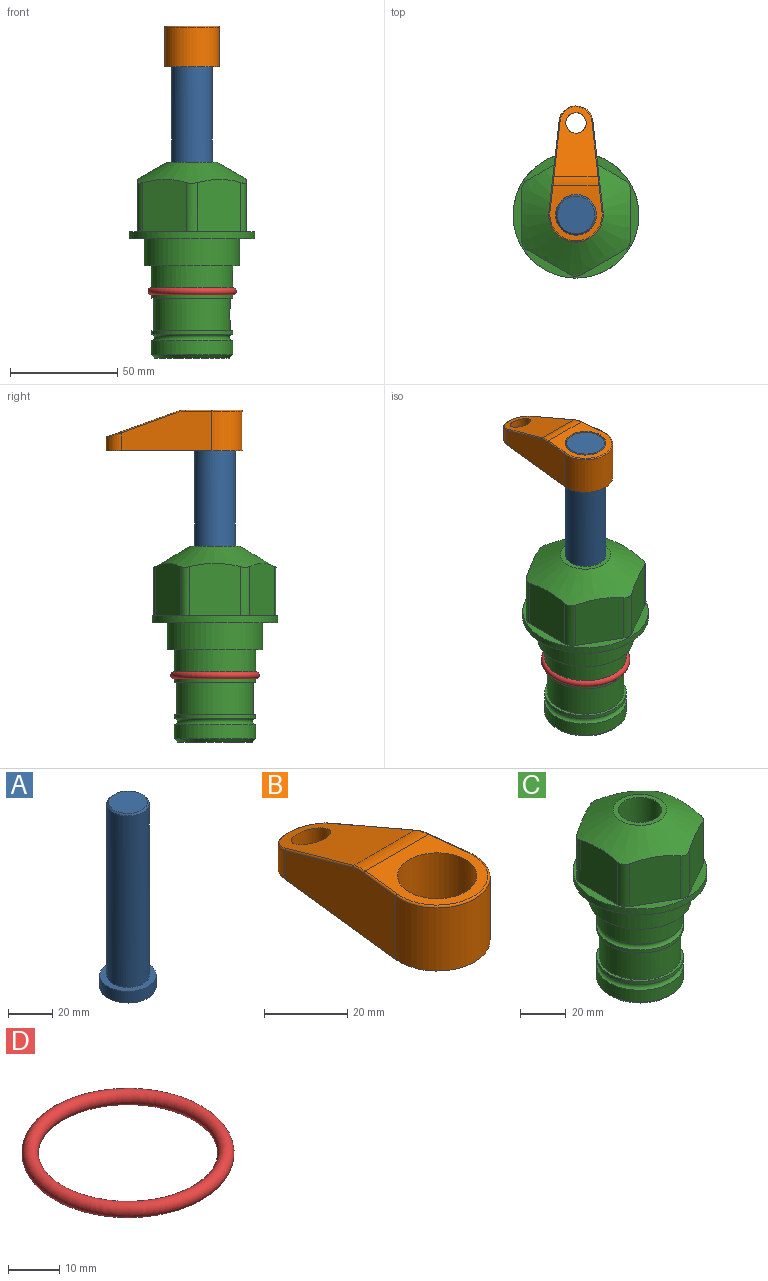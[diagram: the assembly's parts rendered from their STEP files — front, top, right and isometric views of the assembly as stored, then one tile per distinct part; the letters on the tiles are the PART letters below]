
ASSEMBLY  parts=4 mates=2
PART A: 6 faces, bbox 25.4x25.4x101.6 mm
  f0: plane 17.46x17.46mm, normal (0,0,1), area 239.5mm2, adj f5
  f1: plane 25.4x25.4mm, normal (0,0,-1), area 506.7mm2, adj f2
  f2: cylinder r=12.7mm len=25.4mm, axis (0,0,1), area 506.7mm2, adj f1,f3
  f3: plane 25.4x25.4mm, normal (0,0,1), area 221.7mm2, adj f2,f4
  f4: cylinder r=9.53mm len=94.46mm, axis (0,0,1), area 5653mm2, adj f3,f5
  f5: cone r=8.73mm half-angle=45deg, axis (0,0,-1), area 64.4mm2, adj f0,f4
PART B: 44 faces, bbox 27.5x64.5x19.1 mm
  f0: plane 2.3x0.95mm, normal (0,0,-1), area 1mm2, adj f25,f30,f34
  f1: plane 63.5x25.4mm, normal (0,0,-1), area 561.7mm2, adj f2,f3,f4,f5,f6,f7,f19,f20
  f2: cylinder r=12.7mm len=25.4mm, axis (0,0,-1), area 792.2mm2, adj f1,f3,f5,f13
  f3: plane 42.33x18.54mm, normal (0.99,0.11,0), area 647mm2, adj f1,f2,f4,f11,f12,f14
  f4: cylinder r=7.94mm len=15.78mm, axis (0,0,-1), area 158.6mm2, adj f1,f3,f5,f16
  f5: plane 42.33x18.54mm, normal (-0.99,0.11,0), area 647mm2, adj f1,f2,f4,f15,f17,f18
  f6: cylinder r=9.53mm len=19.05mm, axis (0,0,-1), area 1140.1mm2, adj f1,f8
  f7: cylinder r=4.76mm len=10.98mm, axis (0,0,-1), area 276.1mm2, adj f1,f9
  f8: plane 25.83x24.38mm, normal (0,0,1), area 262.2mm2, adj f6,f10,f11,f13,f15
  f9: plane 32.49x20.55mm, normal (0,0.34,0.94), area 489.9mm2, adj f7,f10,f14,f16,f18
  f10: cylinder r=12.7mm len=21.49mm, axis (-1,0,0), area 93.2mm2, adj f8,f9,f12,f17
  f11: cylinder r=0.51mm len=12.34mm, axis (0.11,-0.99,0), area 9.9mm2, adj f3,f8,f12,f13
  f12: bspline ~7.62x1.64mm, area 3.5mm2, adj f3,f10,f11,f14
  f13: torus R=12.19mm, axis (0,0,1), area 33.6mm2, adj f2,f8,f11,f15
  f14: cylinder r=0.51mm len=26.01mm, axis (0.1,-0.93,0.34), area 21.6mm2, adj f3,f9,f12,f16
  f15: cylinder r=0.51mm len=12.34mm, axis (0.11,0.99,0), area 9.9mm2, adj f5,f8,f13,f17
  f16: bspline ~15.78x7.05mm, area 15.7mm2, adj f4,f9,f14,f18
  f17: bspline ~7.62x1.64mm, area 3.5mm2, adj f5,f10,f15,f18
  f18: cylinder r=0.51mm len=26.01mm, axis (0.1,0.93,-0.34), area 21.6mm2, adj f5,f9,f16,f17
  f19: plane 21.6x14.29mm, normal (-0.99,-0.11,0), area 242.6mm2, adj f1,f26,f28,f34,f36,f38
  f20: plane 21.6x14.29mm, normal (0.99,-0.11,0), area 242.6mm2, adj f1,f27,f29,f37,f39,f41
  f21: cylinder r=12.7mm len=14.29mm, axis (0,0,-1), area 173.2mm2, adj f1,f26,f27,f30,f31,f33
  f22: cylinder r=7.94mm len=7.63mm, axis (0,0,-1), area 53.8mm2, adj f1,f28,f29,f42
  f23: plane 2.3x0.95mm, normal (0,0,-1), area 1mm2, adj f25,f33,f37
  f24: plane 17.94x12.32mm, normal (0,-0.34,-0.94), area 191.2mm2, adj f25,f38,f41,f42
  f25: cylinder r=9.53mm len=12.93mm, axis (-1,0,0), area 37.5mm2, adj f0,f23,f24,f31,f36,f39
  f26: cylinder r=1.59mm len=14.29mm, axis (0,0,-1), area 49mm2, adj f1,f19,f21,f32
  f27: cylinder r=1.59mm len=14.29mm, axis (0,0,-1), area 49mm2, adj f1,f20,f21,f35
  f28: cylinder r=1.59mm len=7.28mm, axis (0,0,-1), area 22.1mm2, adj f1,f19,f22,f40
  f29: cylinder r=1.59mm len=7.28mm, axis (0,0,-1), area 22.1mm2, adj f1,f20,f22,f43
  f30: torus R=14.29mm, axis (0,0,1), area 5.8mm2, adj f0,f21,f31,f32
  f31: bspline ~11.06x2.73mm, area 20.8mm2, adj f21,f25,f30,f33
  f32: sphere r=1.59mm, area 5.4mm2, adj f26,f30,f34
  f33: torus R=14.29mm, axis (0,0,1), area 5.8mm2, adj f21,f23,f31,f35
  f34: cylinder r=1.59mm len=1.68mm, axis (-0.11,0.99,0), area 2.4mm2, adj f0,f19,f32,f36
  f35: sphere r=1.59mm, area 5.4mm2, adj f27,f33,f37
  f36: bspline ~5.82x2.33mm, area 7.7mm2, adj f19,f25,f34,f38
  f37: cylinder r=1.59mm len=1.68mm, axis (0.11,0.99,0), area 2.4mm2, adj f20,f23,f35,f39
  f38: cylinder r=1.59mm len=18.33mm, axis (0.1,-0.93,0.34), area 46.7mm2, adj f19,f24,f36,f40
  f39: bspline ~5.82x2.33mm, area 7.7mm2, adj f20,f25,f37,f41
  f40: sphere r=1.59mm, area 3.6mm2, adj f28,f38,f42
  f41: cylinder r=1.59mm len=18.33mm, axis (0.1,0.93,-0.34), area 46.7mm2, adj f20,f24,f39,f43
  f42: bspline ~8.31x1.84mm, area 15.3mm2, adj f22,f24,f40,f43
  f43: sphere r=1.59mm, area 3.6mm2, adj f29,f41,f42
PART C: 36 faces, bbox 58.7x58.7x91.2 mm
  f0: cylinder r=17.78mm len=35.56mm, axis (0,0,1), area 1670.8mm2, adj f23,f24,f31
  f1: cylinder r=19.05mm len=38.1mm, axis (0,0,1), area 1191.9mm2, adj f26,f27,f30
  f2: plane 58.66x58.66mm, normal (0,0,-1), area 1150.6mm2, adj f3,f28
  f3: cylinder r=29.33mm len=58.66mm, axis (0,0,-1), area 585.1mm2, adj f2,f4
  f4: plane 58.66x58.66mm, normal (0,0,1), area 475.9mm2, adj f3,f5,f6,f7,f8,f9,f10,f11
  f5: plane 24.5x20.32mm, normal (0.5,-0.87,0), area 562.8mm2, adj f4,f15,f16,f17
  f6: plane 24.5x20.32mm, normal (-0.5,-0.87,0), area 562.8mm2, adj f4,f14,f15,f17
  f7: plane 24.5x23.48mm, normal (-1,0,0), area 562.8mm2, adj f4,f13,f14,f17
  f8: plane 24.5x20.32mm, normal (-0.5,0.87,0), area 562.8mm2, adj f4,f12,f13,f17
  f9: plane 24.5x20.32mm, normal (0.5,0.87,0), area 562.8mm2, adj f4,f11,f12,f17
  f10: plane 24.5x23.48mm, normal (1,0,0), area 562.8mm2, adj f4,f11,f16,f17
  f11: cylinder r=5.08mm len=23.01mm, axis (0,0,-1), area 121.2mm2, adj f4,f9,f10,f17
  f12: cylinder r=5.08mm len=23.01mm, axis (0,0,-1), area 121.2mm2, adj f4,f8,f9,f17
  f13: cylinder r=5.08mm len=23.01mm, axis (0,0,-1), area 121.2mm2, adj f4,f7,f8,f17
  f14: cylinder r=5.08mm len=23.01mm, axis (0,0,-1), area 121.2mm2, adj f4,f6,f7,f17
  f15: cylinder r=5.08mm len=23.01mm, axis (0,0,-1), area 121.2mm2, adj f4,f5,f6,f17
  f16: cylinder r=5.08mm len=23.01mm, axis (0,0,-1), area 121.2mm2, adj f4,f5,f10,f17
  f17: cone r=11.73mm half-angle=60deg, axis (0,0,-1), area 2071.8mm2, adj f5,f6,f7,f8,f9,f10,f11,f12
  f18: plane 23.46x23.46mm, normal (0,0,1), area 147.4mm2, adj f17,f35
  f19: plane 34.93x34.93mm, normal (0,0,-1), area 958mm2, adj f29
  f20: cylinder r=19.05mm len=38.1mm, axis (0,0,1), area 760.1mm2, adj f21,f29
  f21: torus R=19.05mm, axis (0,0,1), area 565.3mm2, adj f20,f22
  f22: cylinder r=19.05mm len=38.1mm, axis (0,0,1), area 190mm2, adj f21,f23
  f23: plane 38.1x38.1mm, normal (0,0,1), area 146.9mm2, adj f0,f22
  f24: plane 38.1x38.1mm, normal (0,0,-1), area 146.9mm2, adj f0,f25
  f25: cylinder r=19.05mm len=38.1mm, axis (0,0,1), area 190mm2, adj f24,f26
  f26: torus R=19.05mm, axis (0,0,1), area 565.3mm2, adj f1,f25
  f27: plane 44.45x44.45mm, normal (0,0,-1), area 411.7mm2, adj f1,f28
  f28: cylinder r=22.23mm len=44.45mm, axis (0,0,1), area 1773.5mm2, adj f2,f27
  f29: cone r=19.05mm half-angle=45deg, axis (0,0,1), area 257.5mm2, adj f19,f20
  f30: cylinder r=3.17mm len=6.75mm, axis (-1,0,0), area 128mm2, adj f1,f33
  f31: cylinder r=3.17mm len=6.35mm, axis (-1,0,0), area 102.5mm2, adj f0,f33
  f32: plane 25.4x25.4mm, normal (0,0,1), area 506.7mm2, adj f33
  f33: cylinder r=12.7mm len=66.42mm, axis (0,0,-1), area 5236.2mm2, adj f30,f31,f32,f34
  f34: cone r=9.53mm half-angle=30deg, axis (0,0,-1), area 443.4mm2, adj f33,f35
  f35: cylinder r=9.53mm len=19.05mm, axis (0,0,-1), area 849mm2, adj f18,f34
PART D: 1 faces, bbox 44.7x44.7x3.2 mm
  f0: torus R=19.05mm, axis (0,0,1), area 1193.9mm2
PLACE A t=(0,0,25.54)mm
PLACE B t=(0,0,80.15)mm
PLACE C at identity fixed
PLACE D at identity
MATE slider A.f2 <-> C.f0  axis (0,0,1) through (0,0,51.18)mm
MATE fastened B.f2 <-> A.f2  axis (0,0,-1) through (0,0,99.2)mm
